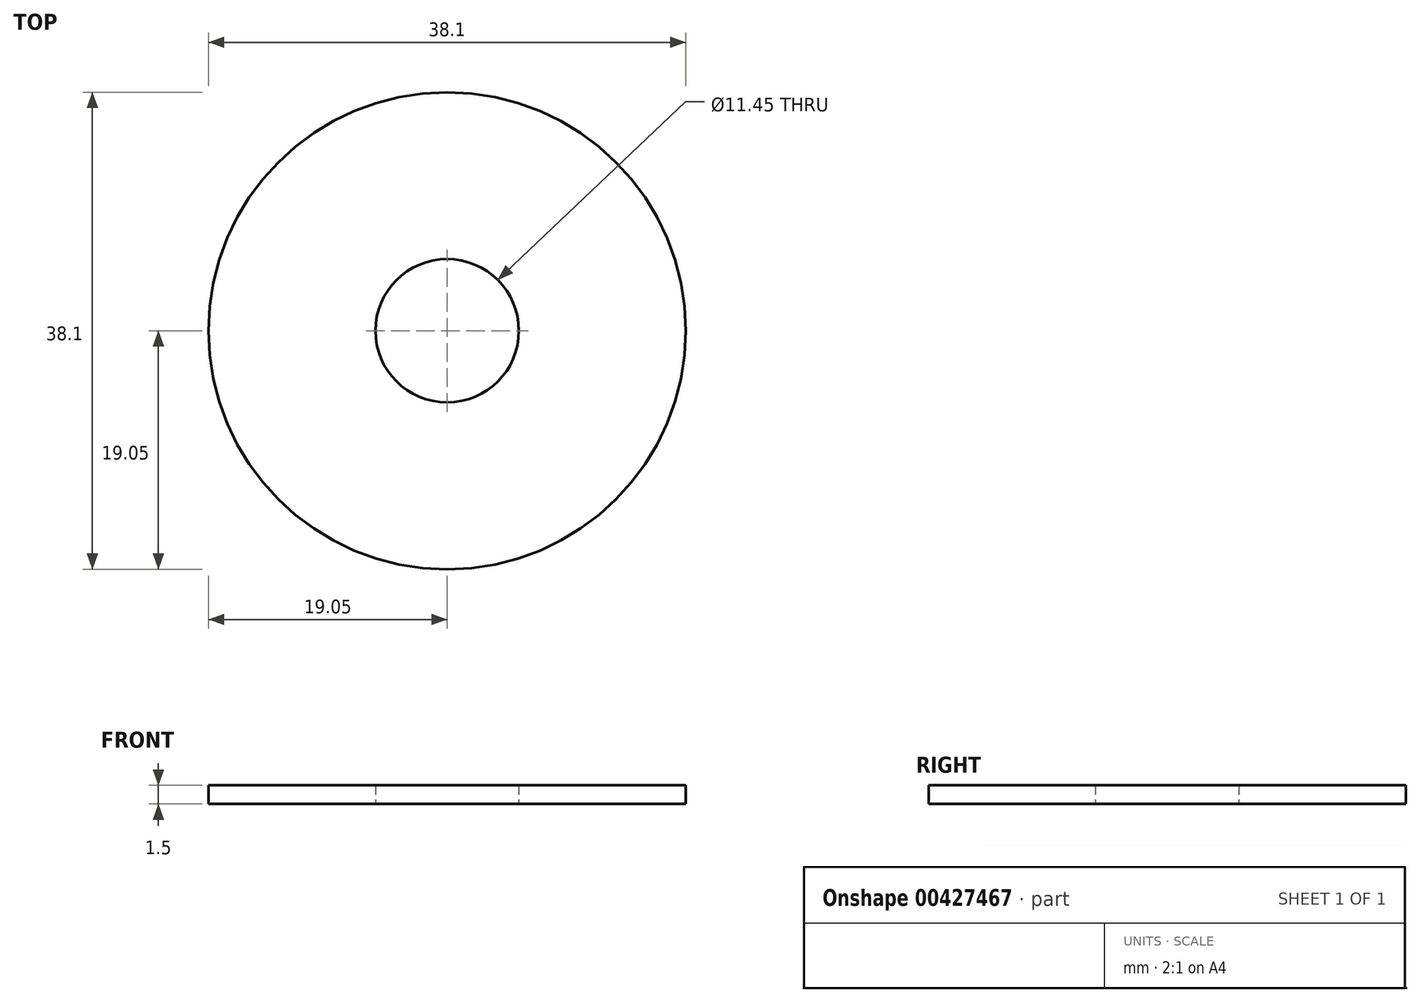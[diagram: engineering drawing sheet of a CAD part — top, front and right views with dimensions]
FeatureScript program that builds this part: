
annotation { "Feature Type Name" : "Feature", "Feature Type Description" : "" }
export const myFeature = defineFeature(function(context is Context, id is Id, definition is map)
    precondition{}
    {
        {
            var Q0;
            Q0=qCreatedBy(makeId("Top.planeOp"),FACE);
            var sketch = newSketch(context, id + "F0", { "sketchPlane" : qUnion([Q0])});
            skCircle(sketch, "E0", {"center": v(0, 0) * mm, "radius": 5.73 * mm});
            skCircle(sketch, "E1", {"center": v(0, 0) * mm, "radius": 19.05 * mm});
            skSolve(sketch);
        }
        {
            var Q0;
            Q0 = qSketchRegion(id + "F0", true);
            extrude(context, id + "F1", {"entities" : qUnion([Q0]), "depth" : 1.5 * mm});
        }
    });
